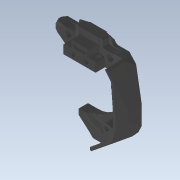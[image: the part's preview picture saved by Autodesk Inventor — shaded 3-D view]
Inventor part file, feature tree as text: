
AUTODESK INVENTOR PART (.ipt)
format: ipt  version: 2022.1 (Build 261234020, 234B)  size: 1,084,416 bytes
history: native  units: mm
features: sketch x3, extrude x2, delete_face x2, chamfer x2, direct_edit x1, hole x1, imported_body x1, move_body x1
ambient origin geometry x8: Origin, YZ Plane, XZ Plane, XY Plane, X Axis, Y Axis, Z Axis, Center Point
bodies: Volumenkörper1 (feature_tree)
feature tree (13):
  direct_edit  "Direktbearbeitung1"
  extrude  "Extrusion1"  Depth=10.0mm
  delete_face  "Fläche löschen1"
  chamfer  "Fase1"  Distance=10.0mm
  delete_face  "Fläche löschen2"
  extrude  "Extrusion2"  Depth=10.0mm TaperAngle=0.0deg
  hole  "Bohrung1"  [1 undecoded]
  chamfer  "Fase2"  [1 undecoded]
  sketch  "Skizze1"  dims[d0=0.0mm d1=0.0mm d2=0.2mm d3=3.1mm d4=10.0mm d5=0.0mm]
  sketch  "Skizze2"  dims[d6=0.4mm d7=2.0mm d8=45.0deg d9=10.0mm d10=0.0mm]
  sketch  "Skizze3"  dims[d11=3.399999mm d12=3.0mm d13=6.0mm d14=4.7mm d15=5.2mm d16=90.0deg d17=8.0mm d18=20.594885mm d19=0.4mm d20=2.0mm d21=45.0deg]
  imported_body  "Basis1"
  move_body  "Verschieben1"
note: 2 required parameter values undecoded (feature->parameter linkage not recoverable at this tier; creation-order binding heuristic only, values carry confidence <= 0.55)
